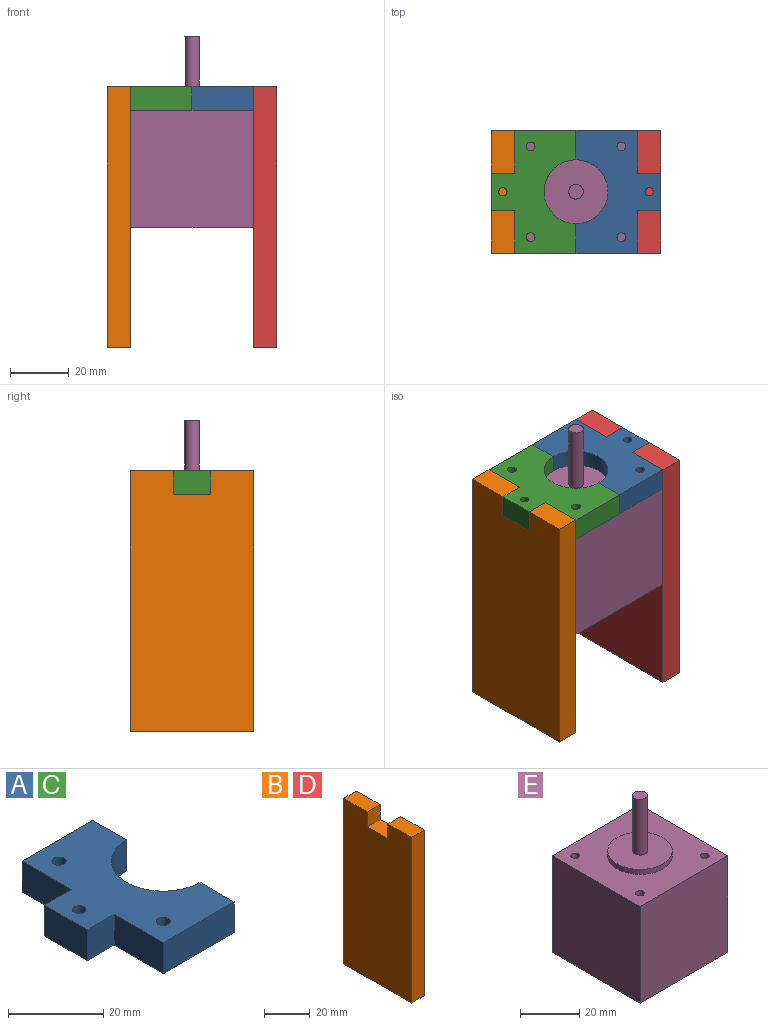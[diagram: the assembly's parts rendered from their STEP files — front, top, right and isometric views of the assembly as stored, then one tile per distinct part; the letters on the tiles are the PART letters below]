
ASSEMBLY  parts=5 mates=6
PART A: 15 faces, bbox 29x42x8 mm
  f0: plane 10.08x7.95mm, normal (1,0,0), area 80.2mm2, adj f3,f9,f10,f11
  f1: plane 7.95x7.95mm, normal (0,-1,0), area 63.2mm2, adj f2,f8,f9,f10
  f2: plane 14.66x7.95mm, normal (-1,0,0), area 116.5mm2, adj f1,f3,f9,f10
  f3: plane 21.01x7.95mm, normal (0,-1,0), area 167mm2, adj f0,f2,f9,f10
  f4: plane 10.08x7.95mm, normal (1,0,0), area 80.2mm2, adj f5,f9,f10,f11
  f5: plane 21.01x7.95mm, normal (0,1,0), area 167mm2, adj f4,f6,f9,f10
  f6: plane 14.66x7.95mm, normal (-1,0,0), area 116.5mm2, adj f5,f7,f9,f10
  f7: plane 7.95x7.95mm, normal (0,1,0), area 63.2mm2, adj f6,f8,f9,f10
  f8: plane 12.7x7.95mm, normal (-1,0,0), area 101mm2, adj f1,f7,f9,f10
  f9: plane 42.01x28.96mm, normal (0,0,1), area 775.6mm2, adj f0,f1,f2,f3,f4,f5,f6,f7
  f10: plane 42.01x28.96mm, normal (0,0,-1), area 775.6mm2, adj f0,f1,f2,f3,f4,f5,f6,f7
  f11: cylinder r=10.92mm len=21.84mm, axis (0,0,1), area 272.8mm2, adj f0,f4,f9,f10
  f12: cylinder r=1.5mm len=7.95mm, axis (0,0,1), area 74.9mm2, adj f9,f10
  f13: cylinder r=1.42mm len=7.95mm, axis (0,0,1), area 71.1mm2, adj f9,f10
  f14: cylinder r=1.5mm len=7.95mm, axis (0,0,1), area 74.9mm2, adj f9,f10
PART B: 10 faces, bbox 8x42x88.9 mm
  f0: plane 14.66x7.95mm, normal (0,0,1), area 116.5mm2, adj f1,f2,f3,f7
  f1: plane 88.9x42.01mm, normal (-1,0,0), area 3633.9mm2, adj f0,f3,f4,f5,f6,f7,f8,f9
  f2: plane 88.9x42.01mm, normal (1,0,0), area 3633.9mm2, adj f0,f3,f4,f5,f6,f7,f8,f9
  f3: plane 88.9x7.95mm, normal (0,1,0), area 706.8mm2, adj f0,f1,f2,f5
  f4: plane 88.9x7.95mm, normal (0,-1,0), area 706.8mm2, adj f1,f2,f5,f6
  f5: plane 42.01x7.95mm, normal (0,0,-1), area 334mm2, adj f1,f2,f3,f4
  f6: plane 14.66x7.95mm, normal (0,0,1), area 116.5mm2, adj f1,f2,f4,f8
  f7: plane 7.95x7.95mm, normal (0,-1,0), area 63.2mm2, adj f0,f1,f2,f9
  f8: plane 7.95x7.95mm, normal (0,1,0), area 63.2mm2, adj f1,f2,f6,f9
  f9: plane 12.7x7.95mm, normal (0,0,1), area 101mm2, adj f1,f2,f7,f8
PART C: same geometry as A
PART D: same geometry as B
PART E: 18 faces, bbox 42x42x65.1 mm
  f0: plane 42x42mm, normal (0,0,1), area 1361mm2, adj f1,f2,f3,f4,f6,f10,f12,f14
  f1: plane 42x40mm, normal (0,1,0), area 1680mm2, adj f0,f2,f4,f5
  f2: plane 42x40mm, normal (-1,0,0), area 1680mm2, adj f0,f1,f3,f5
  f3: plane 42x40mm, normal (0,-1,0), area 1680mm2, adj f0,f2,f4,f5
  f4: plane 42x40mm, normal (1,0,0), area 1680mm2, adj f0,f1,f3,f5
  f5: plane 42x42mm, normal (0,0,-1), area 1764mm2, adj f1,f2,f3,f4
  f6: cylinder r=10.92mm len=21.84mm, axis (0,0,-1), area 142.1mm2, adj f0,f7
  f7: plane 21.84x21.84mm, normal (0,0,1), area 355.1mm2, adj f6,f8
  f8: cylinder r=2.5mm len=23mm, axis (0,0,-1), area 361.3mm2, adj f7,f9
  f9: plane 5x5mm, normal (0,0,1), area 19.6mm2, adj f8
  f10: cylinder r=1.5mm len=4.5mm, axis (0,0,1), area 42.4mm2, adj f0,f11
  f11: plane 3x3mm, normal (0,0,1), area 7.1mm2, adj f10
  f12: cylinder r=1.5mm len=4.5mm, axis (0,0,1), area 42.4mm2, adj f0,f13
  f13: plane 3x3mm, normal (0,0,1), area 7.1mm2, adj f12
  f14: cylinder r=1.5mm len=4.5mm, axis (0,0,1), area 42.4mm2, adj f0,f15
  f15: plane 3x3mm, normal (0,0,1), area 7.1mm2, adj f14
  f16: cylinder r=1.5mm len=4.5mm, axis (0,0,1), area 42.4mm2, adj f0,f17
  f17: plane 3x3mm, normal (0,0,1), area 7.1mm2, adj f16
PLACE A rot(axis=(0,0,1),180deg) t=(-13.2,-19.24,32.9)mm
PLACE B t=(-45.53,8.67,40.85)mm
PLACE C t=(-55.21,22.77,32.9)mm
PLACE D rot(axis=(0,0,1),180deg) t=(-22.88,-5.14,40.85)mm
PLACE E t=(-34.2,1.77,-7.1)mm
MATE planar C.f6 <-> B.f2  axis (-1,0,0) through (-55.21,15.44,36.87)mm
MATE cylindrical C.f11 <-> E.f6  axis (0,0,1) through (-34.2,1.77,32.9)mm
MATE planar C.f7 <-> B.f7  axis (0,1,0) through (-59.18,8.12,36.87)mm
MATE planar A.f6 <-> D.f2  axis (1,0,0) through (-13.2,-11.91,36.87)mm
MATE cylindrical A.f11 <-> E.f6  axis (0,0,-1) through (-34.2,1.77,32.9)mm
MATE planar A.f7 <-> D.f7  axis (0,-1,0) through (-9.22,-4.58,36.87)mm
